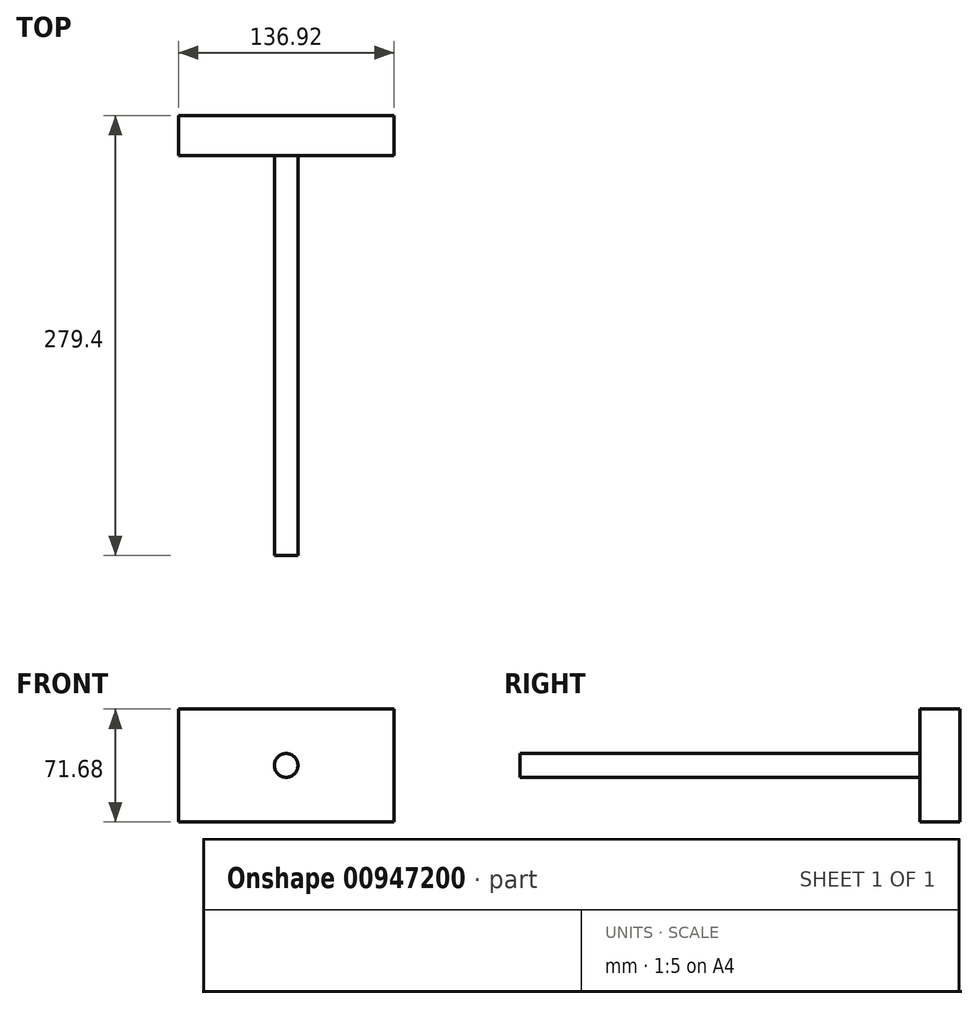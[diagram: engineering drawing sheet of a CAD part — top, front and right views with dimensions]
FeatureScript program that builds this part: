
annotation { "Feature Type Name" : "Feature", "Feature Type Description" : "" }
export const myFeature = defineFeature(function(context is Context, id is Id, definition is map)
    precondition{}
    {
        {
            var Q0;
            Q0=qCreatedBy(makeId("Front.planeOp"),FACE);
            var sketch = newSketch(context, id + "F0", { "sketchPlane" : qUnion([Q0])});
            skCircle(sketch, "E0", {"center": v(0, 0) * mm, "radius": 7.53 * mm});
            skSolve(sketch);
        }
        {
            var Q0;
            Q0=makeQuery(id+"F0.imprint","IMPRINT",FACE,{"disambiguationData":[TD([[makeQuery(id+"F0.imprint","IMPRINT",EDGE,{"derivedFrom":sQuery(id+"F0.wireOp",EDGE,"E0")}),1.0]])]});
            extrude(context, id + "F1", {"entities" : qUnion([Q0]), "depth" : 254 * mm, "offsetDistance" : 25.4 * mm});
        }
        {
            var Q0;
            Q0=qCreatedBy(makeId("Front.planeOp"),FACE);
            var sketch = newSketch(context, id + "F2", { "sketchPlane" : qUnion([Q0])});
            skLineSegment(sketch, "E1.bottom", {"start": v(0, 0) * mm, "end": v(68.46, 0) * mm});
            skLineSegment(sketch, "E1.top", {"start": v(0, 35.84) * mm, "end": v(68.46, 35.84) * mm});
            skLineSegment(sketch, "E1.left", {"start": v(0, 0) * mm, "end": v(0, 35.84) * mm});
            skLineSegment(sketch, "E1.right", {"start": v(68.46, 0) * mm, "end": v(68.46, 35.84) * mm});
            skLineSegment(sketch, "E2.MirrorCS", {"start": v(-68.46, 0) * mm, "end": v(-68.46, 35.84) * mm});
            skLineSegment(sketch, "E3.MirrorCS", {"start": v(0, 35.84) * mm, "end": v(-68.46, 35.84) * mm});
            skLineSegment(sketch, "E4.MirrorCS", {"start": v(0, 0) * mm, "end": v(-68.46, 0) * mm});
            skLineSegment(sketch, "E5.MirrorCS", {"start": v(0, 0) * mm, "end": v(0, -35.84) * mm});
            skLineSegment(sketch, "E6.MirrorCS", {"start": v(0, -35.84) * mm, "end": v(68.46, -35.84) * mm});
            skLineSegment(sketch, "E7.MirrorCS", {"start": v(68.46, 0) * mm, "end": v(68.46, -35.84) * mm});
            skLineSegment(sketch, "E8.MirrorCS", {"start": v(0, -35.84) * mm, "end": v(-68.46, -35.84) * mm});
            skLineSegment(sketch, "E9.MirrorCS", {"start": v(-68.46, 0) * mm, "end": v(-68.46, -35.84) * mm});
            skSolve(sketch);
        }
        {
            var Q0;
            Q0=makeQuery(id+"F2.imprint","IMPRINT",FACE,{"disambiguationData":[TD([[makeQuery(id+"F2.imprint","IMPRINT",EDGE,{"derivedFrom":sQuery(id+"F2.wireOp",EDGE,"E1.bottom")}),-1.0]])]});
            var Q1;
            Q1=makeQuery(id+"F2.imprint","IMPRINT",FACE,{"disambiguationData":[TD([[makeQuery(id+"F2.imprint","IMPRINT",EDGE,{"derivedFrom":sQuery(id+"F2.wireOp",EDGE,"E1.bottom")}),1.0]])]});
            var Q2;
            Q2=makeQuery(id+"F2.imprint","IMPRINT",FACE,{"disambiguationData":[TD([[makeQuery(id+"F2.imprint","IMPRINT",EDGE,{"derivedFrom":sQuery(id+"F2.wireOp",EDGE,"E4.MirrorCS")}),1.0]])]});
            var Q3;
            Q3=makeQuery(id+"F2.imprint","IMPRINT",FACE,{"disambiguationData":[TD([[makeQuery(id+"F2.imprint","IMPRINT",EDGE,{"derivedFrom":sQuery(id+"F2.wireOp",EDGE,"E1.left")}),1.0]])]});
            extrude(context, id + "F3", {"entities" : qUnion([Q0, Q1, Q2, Q3]), "operationType" : NewBodyOperationType.ADD, "oppositeDirection" : true, "depth" : 25.4 * mm, "offsetDistance" : 25.4 * mm});
        }
    });
